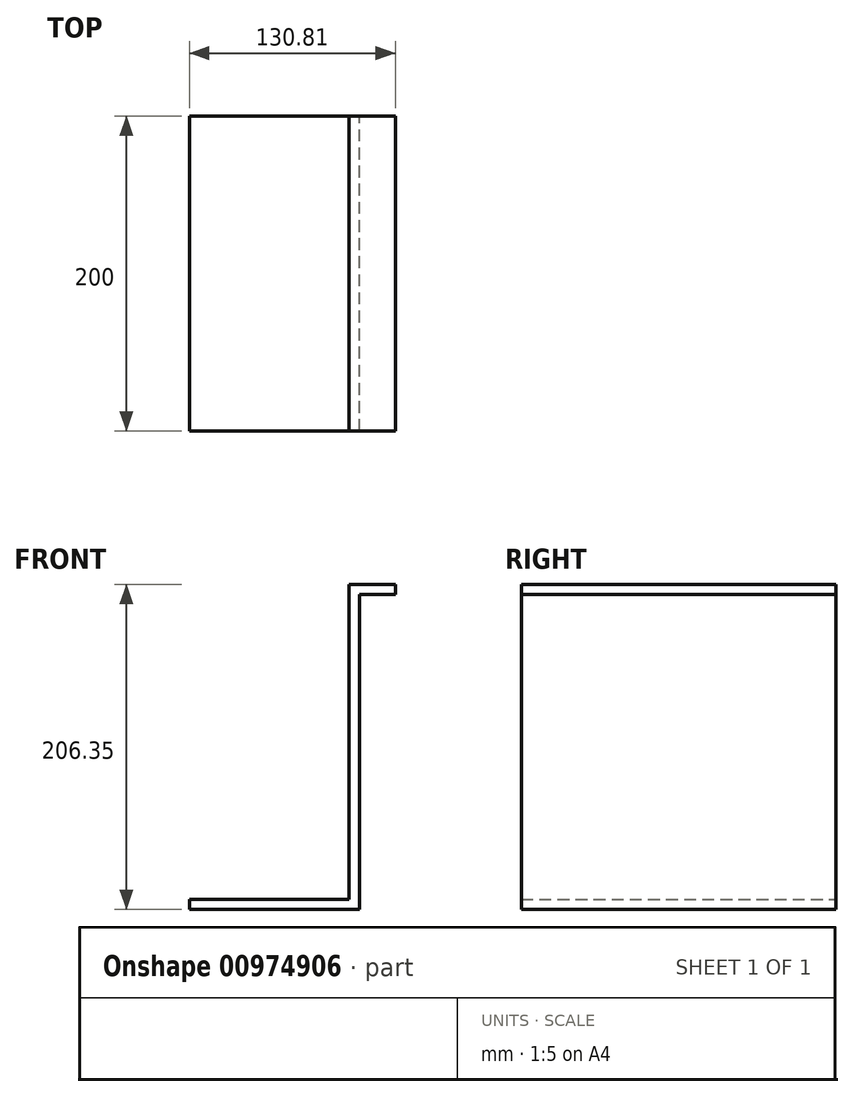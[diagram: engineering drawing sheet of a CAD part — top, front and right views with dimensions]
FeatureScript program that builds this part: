
annotation { "Feature Type Name" : "Feature", "Feature Type Description" : "" }
export const myFeature = defineFeature(function(context is Context, id is Id, definition is map)
    precondition{}
    {
        {
            var Q0;
            Q0=qCreatedBy(makeId("Front.planeOp"),FACE);
            var sketch = newSketch(context, id + "F0", { "sketchPlane" : qUnion([Q0])});
            skLineSegment(sketch, "E0", {"start": v(29.2, 200) * mm, "end": v(0, 200) * mm});
            skLineSegment(sketch, "E1", {"start": v(0, 200) * mm, "end": v(0, 0) * mm});
            skLineSegment(sketch, "E2", {"start": v(0, 0) * mm, "end": v(-101.6, 0) * mm});
            skLineSegment(sketch, "E3", {"start": v(29.2, 200) * mm, "end": v(29.2, 193.65) * mm});
            skLineSegment(sketch, "E4", {"start": v(29.2, 193.65) * mm, "end": v(6.35, 193.65) * mm});
            skLineSegment(sketch, "E5", {"start": v(6.35, 193.65) * mm, "end": v(6.35, -6.35) * mm});
            skLineSegment(sketch, "E6", {"start": v(6.35, -6.35) * mm, "end": v(-101.6, -6.35) * mm});
            skLineSegment(sketch, "E7", {"start": v(-101.6, -6.35) * mm, "end": v(-101.6, 0) * mm});
            skSolve(sketch);
        }
        {
            var Q0;
            Q0 = qSketchRegion(id + "F0", true);
            extrude(context, id + "F1", {"entities" : qUnion([Q0]), "endBound" : BoundingType.SYMMETRIC, "depth" : 200 * mm, "offsetDistance" : 25.4 * mm});
        }
    });
